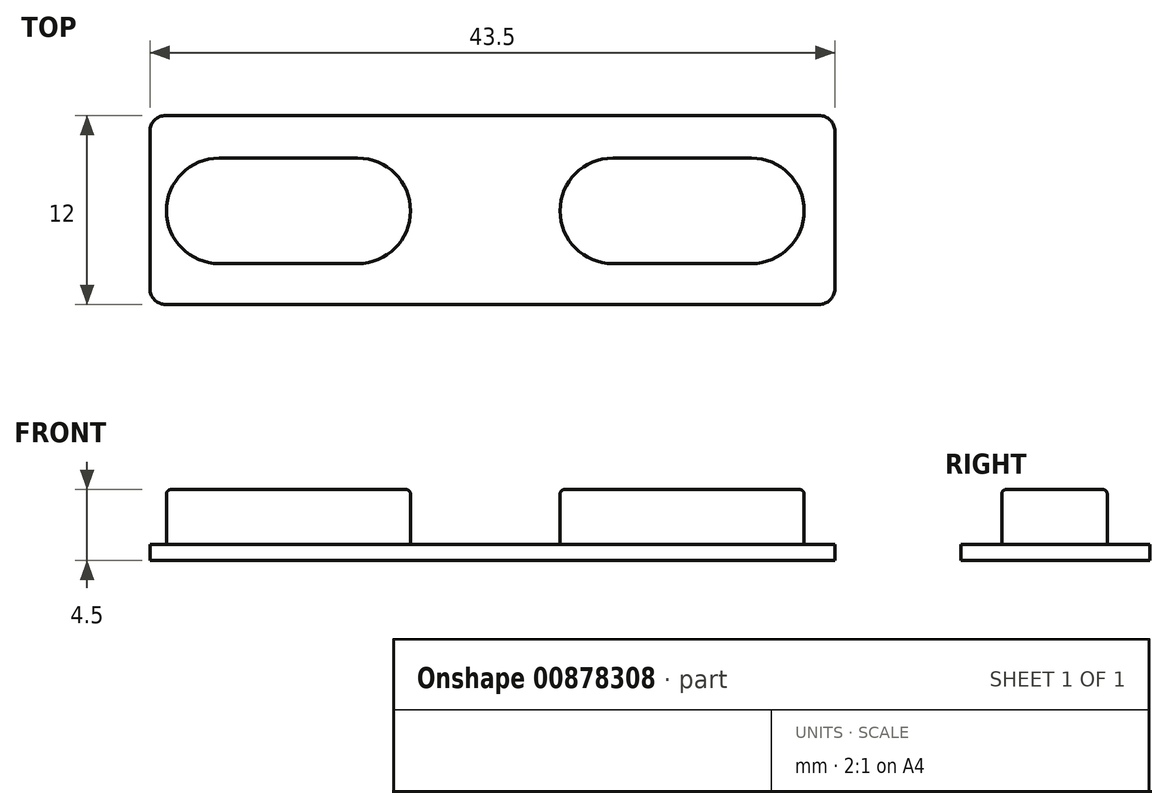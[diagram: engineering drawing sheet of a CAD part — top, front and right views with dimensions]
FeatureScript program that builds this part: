
annotation { "Feature Type Name" : "Feature", "Feature Type Description" : "" }
export const myFeature = defineFeature(function(context is Context, id is Id, definition is map)
    precondition{}
    {
        {
            var Q0;
            Q0=qCreatedBy(makeId("Top.planeOp"),FACE);
            var sketch = newSketch(context, id + "F0", { "sketchPlane" : qUnion([Q0])});
            skLineSegment(sketch, "E0.bottom", {"start": v(-25.9, 6.53) * mm, "end": v(17.6, 6.53) * mm});
            skLineSegment(sketch, "E0.top", {"start": v(-25.9, -5.47) * mm, "end": v(17.6, -5.47) * mm});
            skLineSegment(sketch, "E0.left", {"start": v(-25.9, 6.53) * mm, "end": v(-25.9, -5.47) * mm});
            skLineSegment(sketch, "E0.right", {"start": v(17.6, 6.53) * mm, "end": v(17.6, -5.47) * mm});
            skSolve(sketch);
        }
        {
            var Q0;
            Q0=makeQuery(id+"F0.imprint","IMPRINT",FACE,{"disambiguationData":[TD([[makeQuery(id+"F0.imprint","IMPRINT",EDGE,{"derivedFrom":sQuery(id+"F0.wireOp",EDGE,"E0.bottom")}),-1.0]])]});
            extrude(context, id + "F1", {"entities" : qUnion([Q0]), "depth" : 1 * mm, "offsetDistance" : 25 * mm});
        }
        {
            var Q0;
            Q0=makeQuery(id+"F1.opExtrude","CAP_FACE",FACE,{"disambiguationData":[OSD([sQuery(id+"F0.wireOp",EDGE,"E0.bottom"),sQuery(id+"F0.wireOp",EDGE,"E0.top"),sQuery(id+"F0.wireOp",EDGE,"E0.left"),sQuery(id+"F0.wireOp",EDGE,"E0.right")])],"isStart":false});
            var sketch = newSketch(context, id + "F2", { "sketchPlane" : qUnion([Q0])});
            skLineSegment(sketch, "E1.bottom", {"start": v(-21.5, 3.83) * mm, "end": v(-12.7, 3.83) * mm});
            skLineSegment(sketch, "E1.top", {"start": v(-21.5, -2.87) * mm, "end": v(-12.7, -2.87) * mm});
            skLineSegment(sketch, "E1.left", {"start": v(-21.5, 3.83) * mm, "end": v(-21.5, -2.87) * mm});
            skLineSegment(sketch, "E1.right", {"start": v(-12.7, 3.83) * mm, "end": v(-12.7, -2.87) * mm});
            skArc(sketch, "E2", {"start": v(-21.5, 3.83) * mm, "mid": v(-24.84, 0.48) * mm, "end": v(-21.5, -2.87) * mm});
            skArc(sketch, "E3", {"start": v(-12.7, -2.87) * mm, "mid": v(-9.34, 0.48) * mm, "end": v(-12.7, 3.83) * mm});
            skLineSegment(sketch, "E4.1.0.0", {"start": v(3.5, 3.83) * mm, "end": v(12.3, 3.83) * mm});
            skArc(sketch, "E4.1.0.1", {"start": v(3.5, 3.83) * mm, "mid": v(0.16, 0.48) * mm, "end": v(3.5, -2.87) * mm});
            skLineSegment(sketch, "E4.1.0.2", {"start": v(3.5, -2.87) * mm, "end": v(12.3, -2.87) * mm});
            skArc(sketch, "E4.1.0.3", {"start": v(12.3, -2.87) * mm, "mid": v(15.66, 0.48) * mm, "end": v(12.3, 3.83) * mm});
            skLineSegment(sketch, "E4.direction1", {"start": v(-21.5, 3.83) * mm, "end": v(3.5, 3.83) * mm, "construction": true});
            skSolve(sketch);
        }
        {
            var Q0;
            Q0=makeQuery(id+"F2.imprint","IMPRINT",FACE,{"disambiguationData":[TD([[makeQuery(id+"F2.imprint","IMPRINT",EDGE,{"derivedFrom":sQuery(id+"F2.wireOp",EDGE,"E1.bottom")}),-1.0]])]});
            var Q1;
            Q1=makeQuery(id+"F2.imprint","IMPRINT",FACE,{"disambiguationData":[TD([[makeQuery(id+"F2.imprint","IMPRINT",EDGE,{"derivedFrom":sQuery(id+"F2.wireOp",EDGE,"E1.left")}),-1.0]])]});
            var Q2;
            Q2=makeQuery(id+"F2.imprint","IMPRINT",FACE,{"disambiguationData":[TD([[makeQuery(id+"F2.imprint","IMPRINT",EDGE,{"derivedFrom":sQuery(id+"F2.wireOp",EDGE,"E1.right")}),1.0]])]});
            var Q3;
            Q3=makeQuery(id+"F2.imprint","IMPRINT",FACE,{"disambiguationData":[TD([[makeQuery(id+"F2.imprint","IMPRINT",EDGE,{"derivedFrom":sQuery(id+"F2.wireOp",EDGE,"E4.1.0.0")}),-1.0]])]});
            extrude(context, id + "F3", {"entities" : qUnion([Q0, Q1, Q2, Q3]), "operationType" : NewBodyOperationType.ADD, "depth" : 3.5 * mm, "offsetDistance" : 25 * mm});
        }
        {
            var Q0;
            Q0=makeQuery(id+"F1.opExtrude","SWEPT_EDGE",EDGE,{"disambiguationData":[OSD([sQuery(id+"F0.wireOp",EDGE,"E0.top"),sQuery(id+"F0.wireOp",EDGE,"E0.left")])]});
            var Q1;
            Q1=makeQuery(id+"F1.opExtrude","SWEPT_EDGE",EDGE,{"disambiguationData":[OSD([sQuery(id+"F0.wireOp",EDGE,"E0.bottom"),sQuery(id+"F0.wireOp",EDGE,"E0.right")])]});
            var Q2;
            Q2=makeQuery(id+"F1.opExtrude","SWEPT_EDGE",EDGE,{"disambiguationData":[OSD([sQuery(id+"F0.wireOp",EDGE,"E0.top"),sQuery(id+"F0.wireOp",EDGE,"E0.right")])]});
            var Q3;
            Q3=makeQuery(id+"F1.opExtrude","SWEPT_EDGE",EDGE,{"disambiguationData":[OSD([sQuery(id+"F0.wireOp",EDGE,"E0.bottom"),sQuery(id+"F0.wireOp",EDGE,"E0.left")])]});
            fillet(context, id + "F4", {"entities" : qUnion([Q0, Q1, Q2, Q3]), "radius" : 1 * mm, "tangentPropagation" : true, "allowEdgeOverflow" : false});
        }
        {
            var Q0;
            Q0=makeQuery(id+"F3.opExtrude","CAP_EDGE",EDGE,{"disambiguationData":[OSD([sQuery(id+"F2.wireOp",EDGE,"E1.bottom")])],"isStart":false});
            var Q1;
            Q1=makeQuery(id+"F3.opExtrude","CAP_EDGE",EDGE,{"disambiguationData":[OSD([sQuery(id+"F2.wireOp",EDGE,"E4.1.0.0")])],"isStart":false});
            fillet(context, id + "F5", {"entities" : qUnion([Q0, Q1]), "radius" : 0.3 * mm, "tangentPropagation" : true, "allowEdgeOverflow" : false});
        }
    });
